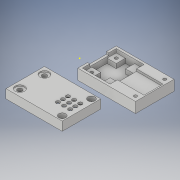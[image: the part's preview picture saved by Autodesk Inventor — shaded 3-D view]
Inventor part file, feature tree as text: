
AUTODESK INVENTOR PART (.ipt)
format: ipt  version: 2019 (Build 230136000, 136)  size: 1,358,848 bytes
history: native  units: mm
features: move_body x28, sketch x26, extrude x24, direct_edit x18, chamfer x2, delete_face x2, split x1
ambient origin geometry x8: Origin, YZ Plane, XZ Plane, XY Plane, X Axis, Y Axis, Z Axis, Center Point
bodies: Solid1 (feature_tree), Solid2 (feature_tree), Solid3 (feature_tree)
feature tree (101):
  sketch  "Sketch1"  dims[d0=21.0mm d1=25.0mm]
  sketch  "Sketch2"  dims[d2=5.0mm d3=0.0mm d4=14.5mm]
  extrude  "Extrusion1"  Depth=25.0mm
  extrude  "Extrusion2"  Depth=5.0mm
  extrude  "Extrusion3"  Depth=1.5mm
  extrude  "Extrusion4"  Depth=6.0mm
  extrude  "Extrusion5"  Depth=6.0mm
  extrude  "Extrusion6"  Depth=6.0mm
  direct_edit  "Direct Edit1"
  extrude  "Extrusion7"  Depth=6.0mm
  direct_edit  "Direct Edit2"
  extrude  "Extrusion8"  Depth=6.0mm
  extrude  "Extrusion9"  Depth=6.0mm
  direct_edit  "Direct Edit3"
  extrude  "Extrusion10"  Depth=6.0mm
  extrude  "Extrusion11"  Depth=6.0mm
  sketch  "Sketch12"  dims[d26=6.0mm d27=1.1mm d28=0.0mm]
  direct_edit  "Direct Edit4"
  extrude  "Extrusion12"  Depth=6.0mm TaperAngle=0.0deg
  sketch  "Sketch14"  dims[d31=2.0mm d32=2.0mm]
  direct_edit  "Direct Edit5"
  direct_edit  "Direct Edit6"
  direct_edit  "Direct Edit7"
  direct_edit  "Direct Edit8"
  direct_edit  "Direct Edit9"
  sketch  "Sketch15"  dims[d33=2.0mm d34=0.0mm d35=1.0mm]
  direct_edit  "Direct Edit10"
  extrude  "Extrusion13"  Depth=2.0mm
  extrude  "Extrusion14"  Depth=2.0mm
  extrude  "Extrusion15"  Depth=1.0mm
  extrude  "Extrusion16"  Depth=1.0mm
  extrude  "Extrusion17"  Depth=1.0mm TaperAngle=0.0deg
  extrude  "Extrusion18"  Depth=0.5mm TaperAngle=0.0deg
  split  "Split1"
  chamfer  "Chamfer1"  Distance=1.0mm
  chamfer  "Chamfer2"  Distance=8.0mm
  extrude  "Extrusion19"  Depth=2.0mm
  delete_face  "Delete Face1"
  delete_face  "Delete Face2"
  direct_edit  "Direct Edit11"
  extrude  "Extrusion20"  Depth=6.0mm
  direct_edit  "Direct Edit12"
  direct_edit  "Direct Edit13"
  sketch  "Sketch23"  dims[d58=16.5mm d59=0.0mm d60=0.0mm d61=0.0mm d62=0.5mm]
  sketch  "Sketch24"  dims[d63=2.0mm d64=16.5mm d65=0.0mm]
  direct_edit  "Direct Edit14"
  direct_edit  "Direct Edit15"
  extrude  "Extrusion21"  Depth=0.5mm TaperAngle=0.0deg
  direct_edit  "Direct Edit16"
  extrude  "Extrusion22"  Depth=2.0mm TaperAngle=0.0deg
  extrude  "Extrusion23"  TaperAngle=0.0deg  [1 undecoded]
  extrude  "Extrusion24"  Depth=1.0mm
  direct_edit  "Direct Edit17"
  direct_edit  "Direct Edit18"
  sketch  "Sketch3"  dims[d5=16.5mm d6=0.0mm d8=1.5mm]
  sketch  "Sketch4"  dims[d9=6.0mm d10=6.0mm]
  sketch  "Sketch5"  dims[d11=6.0mm d12=6.0mm]
  sketch  "Sketch6"  dims[d13=6.0mm d14=6.0mm]
  sketch  "Sketch7"  dims[d15=6.0mm d16=6.0mm]
  sketch  "Sketch8"  dims[d17=4.0mm d18=0.0mm d19=6.0mm]
  sketch  "Sketch9"  dims[d20=6.0mm d21=6.0mm]
  sketch  "Sketch10"  dims[d22=6.0mm d23=6.0mm]
  sketch  "Sketch11"  dims[d24=6.0mm d25=6.0mm]
  sketch  "Sketch13"  dims[d29=2.0mm d30=2.0mm]
  sketch  "Sketch16"  dims[d36=1.0mm d37=1.0mm]
  sketch  "Sketch17"  dims[d38=1.0mm d39=1.0mm d40=0.0mm]
  sketch  "Sketch18"  dims[d41=0.0mm d42=0.0mm d43=0.5mm d45=0.5mm d46=0.0mm]
  sketch  "Sketch19"  dims[d47=25.0mm]
  sketch  "Sketch20"  dims[d48=21.0mm d49=0.0mm d50=0.0mm d51=1.0mm d52=8.0mm d53=0.0mm]
  sketch  "Sketch21"  dims[d54=2.0mm d55=7.25mm]
  sketch  "Sketch22"  dims[d56=14.5mm d57=6.0mm]
  sketch  "Sketch25"  dims[d68=5.0mm d69=0.0mm d70=0.0mm d71=0.0mm d72=-1.0mm]
  sketch  "Sketch26"  dims[d73=12.3mm d74=1.2mm d75=5.0mm d76=0.0mm d77=0.0mm d78=0.0mm d79=5.25mm d80=0.0mm d81=0.0mm d82=5.25mm d83=0.0mm d84=0.0mm d85=5.25mm d86=0.0mm d87=0.0mm d88=5.25mm d89=0.0mm d90=0.0mm d91=2.0mm d92=0.0mm d93=0.0mm d94=13.75mm d96=2.5mm d97=30.0mm d99=3.25mm d100=30.0mm d102=4.0mm d105=5.0mm d106=0.0mm d107=12.5mm d108=10.7mm d109=1.5mm d110=0.0mm d111=12.3mm d112=4.3mm d113=1.5mm d114=0.0mm d115=6.0mm d116=4.86mm d117=6.0mm d118=4.86mm d119=6.0mm d120=6.0mm d121=6.0mm d122=6.0mm d123=3.0mm d124=3.0mm d125=3.0mm d126=3.0mm d127=3.0mm d128=0.0mm d129=6.0mm d130=6.0mm d131=6.0mm d132=6.0mm d133=6.0mm d134=6.0mm d135=5.0mm d136=0.0mm d137=6.0mm d138=6.0mm d139=6.0mm d140=6.0mm d141=2.0mm d142=0.0mm d144=1.0mm d145=2.0mm d146=45.0deg d147=1.0mm d148=2.0mm d149=45.0deg d150=0.6mm d151=0.0mm d152=0.0mm d153=-0.5mm d154=0.0mm d155=0.0mm d156=0.0mm d157=1.5mm d158=0.0mm d159=0.0mm d160=1.5mm d161=8.0mm d162=0.0mm d163=0.0mm d164=0.0mm d165=-0.25mm d166=0.0mm d167=0.0mm d168=-0.25mm d169=0.0mm d170=0.0mm d171=0.25mm d172=0.0mm d173=0.0mm d174=0.25mm d175=6.0mm d176=6.0mm d177=6.0mm d178=6.0mm d179=6.0mm d180=6.0mm d181=6.0mm d182=6.0mm d183=0.0mm d184=0.0mm d185=0.25mm d186=0.0mm d187=0.0mm d188=0.25mm d189=0.0mm d190=0.0mm d191=0.4mm d192=3.0mm d193=3.0mm d194=8.0mm d195=0.0mm d196=0.0mm d197=0.0mm d198=1.0mm d199=0.0mm d200=0.0mm d201=-1.25mm d202=4.5mm d203=4.5mm d204=3.0mm d205=0.0mm d206=2.0mm d207=2.0mm d208=3.0mm d209=0.0mm d210=1.0mm d211=1.0mm d212=1.5mm d213=0.0mm d214=0.0mm d215=0.0mm d216=-0.5mm d217=0.0mm d218=0.0mm d219=-1.2mm d220=0.0mm d221=0.0mm d222=-1.2mm d223=0.0mm d224=0.0mm d225=0.3mm d226=0.0mm d227=0.0mm d228=-1.0mm d229=0.0mm d230=0.0mm d231=1.0mm]
  move_body  "Move1"
  move_body  "Move2"
  move_body  "Move3"
  move_body  "Move4"
  move_body  "Move5"
  move_body  "Move6"
  move_body  "Move7"
  move_body  "Move8"
  move_body  "Move9"
  move_body  "Move10"
  move_body  "Move11"
  move_body  "Move12"
  move_body  "Move13"
  move_body  "Move14"
  move_body  "Move15"
  move_body  "Move16"
  move_body  "Move17"
  move_body  "Move18"
  move_body  "Move19"
  move_body  "Move20"
  move_body  "Move21"
  move_body  "Move22"
  move_body  "Move23"
  move_body  "Move24"
  move_body  "Move25"
  move_body  "Move26"
  move_body  "Move27"
  move_body  "Move28"
note: 1 required parameter value undecoded (feature->parameter linkage not recoverable at this tier; creation-order binding heuristic only, values carry confidence <= 0.55)
